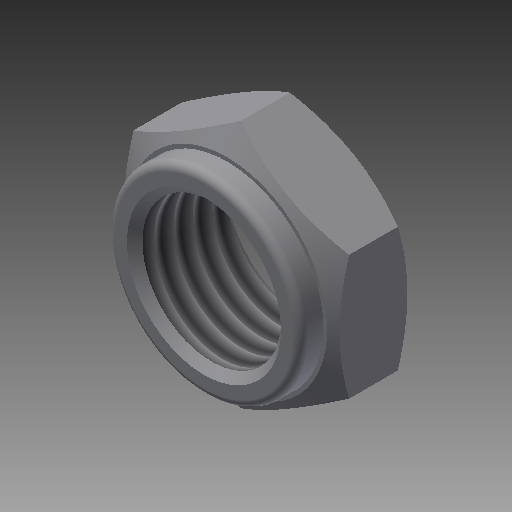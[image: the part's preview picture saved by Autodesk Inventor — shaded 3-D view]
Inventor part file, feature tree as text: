
AUTODESK INVENTOR PART (.ipt)
format: ipt  version: 2019 (Build 230136000, 136)  size: 190,464 bytes
history: native  units: mm
features: extrude x2, sketch x2, other x2, hole x1, thread x1, chamfer x1, revolve x1, fillet x1
ambient origin geometry x8: Origin, YZ Plane, XZ Plane, XY Plane, X Axis, Y Axis, Z Axis, Center Point
bodies: Solido1 (feature_tree)
feature tree (11):
  extrude  "Estrusione1"  Depth=14.0mm
  extrude  "Estrusione2"  Depth=5.0mm TaperAngle=0.0deg
  sketch  "Schizzo3"
  other  "Piano di lavoro1"
  hole  "Foro1"  [1 undecoded]
  thread  "Filettatura1"
  chamfer  "Smusso1"  Distance=12.5mm
  revolve  "Rivoluzione2"
  fillet  "Raccordo1"  [1 undecoded]
  sketch  "Schizzo1"
  other  "Linea chiusa proiettata1"
note: 2 required parameter values undecoded (feature->parameter linkage not recoverable at this tier; creation-order binding heuristic only, values carry confidence <= 0.55)
